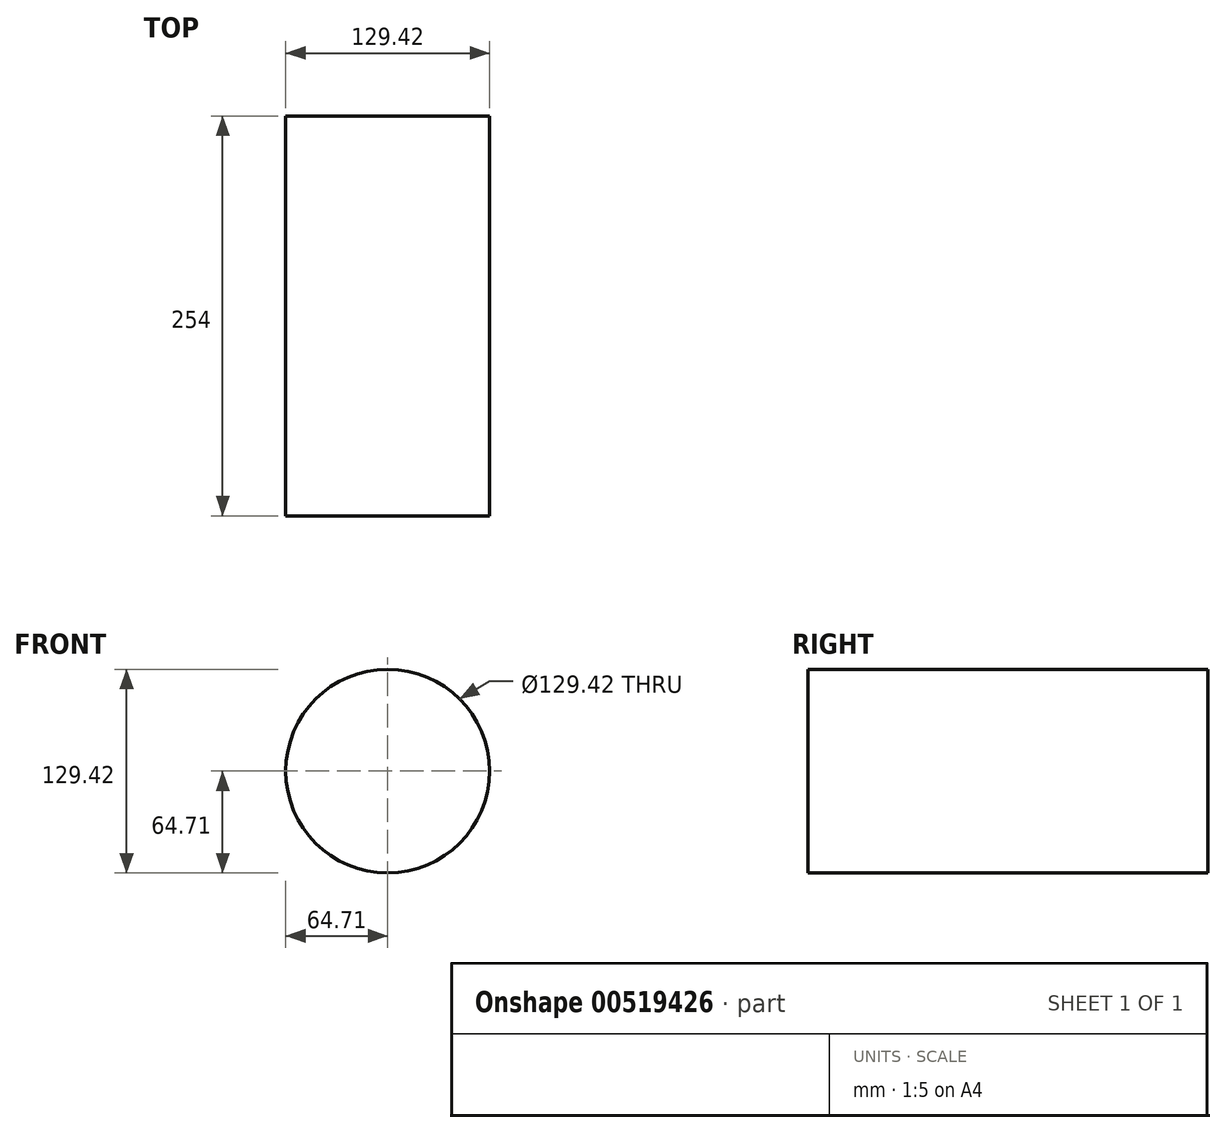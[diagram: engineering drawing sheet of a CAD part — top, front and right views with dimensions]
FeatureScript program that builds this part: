
annotation { "Feature Type Name" : "Feature", "Feature Type Description" : "" }
export const myFeature = defineFeature(function(context is Context, id is Id, definition is map)
    precondition{}
    {
        {
            var Q0;
            Q0=qCreatedBy(makeId("Front.planeOp"),FACE);
            var sketch = newSketch(context, id + "F0", { "sketchPlane" : qUnion([Q0])});
            skCircle(sketch, "E0", {"center": v(0, 0) * mm, "radius": 64.71 * mm});
            skSolve(sketch);
        }
        {
            var Q0;
            Q0=sQuery(id+"F0.wireOp",EDGE,"E0");
            extrude(context, id + "F1", {"bodyType" : ToolBodyType.SURFACE, "surfaceEntities" : qUnion([Q0]), "oppositeDirection" : true, "depth" : 254 * mm, "offsetDistance" : 25.4 * mm});
        }
    });
